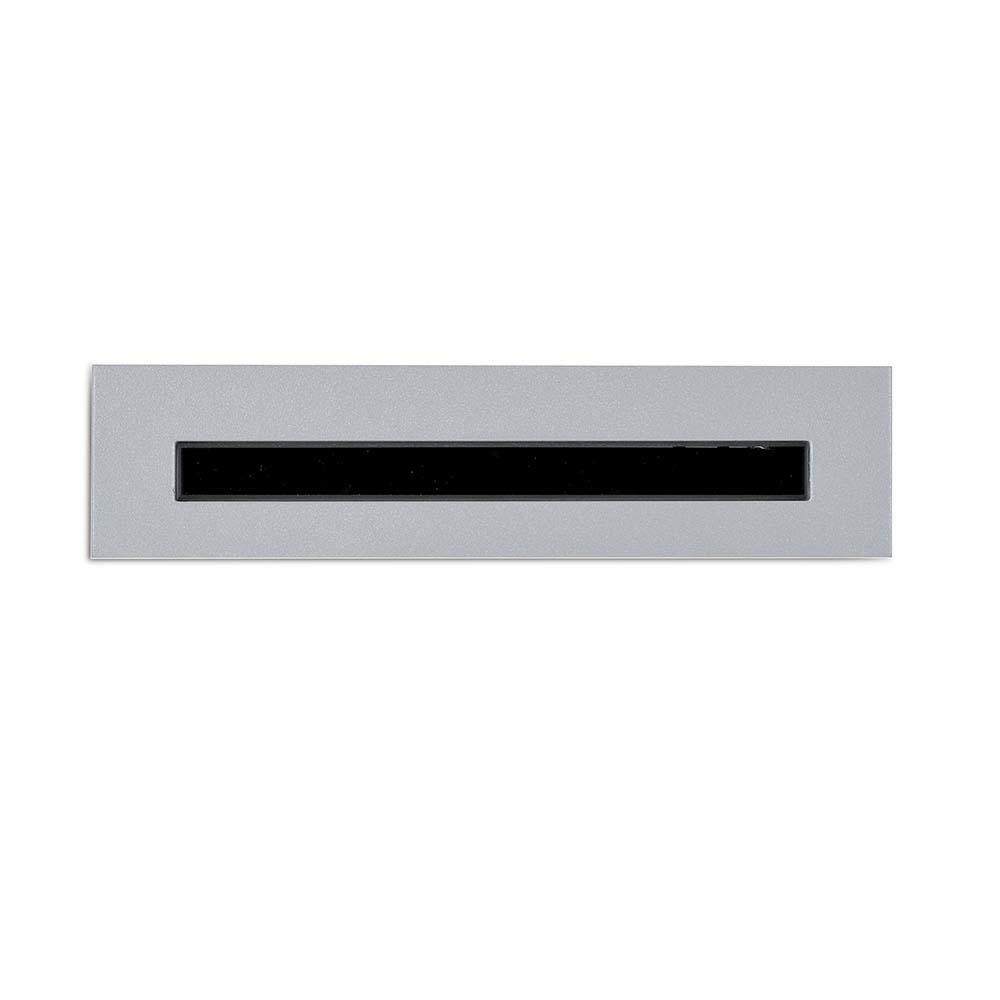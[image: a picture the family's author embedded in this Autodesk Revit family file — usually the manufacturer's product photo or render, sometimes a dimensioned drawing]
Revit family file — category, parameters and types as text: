
# Revit family: Platek_Frame
name_source: partatom
category: Apparecchi per illuminazione
revit_build: Autodesk Revit 2017 (Build: 20160225_1515(x64)
units: mm (PartAtom-declared; Revit-internal decimal feet)

## family parameters
Condiviso = No
Host = Superficie
Punto di calcolo locali = No
Quota connettore circolare = Usa diametro
Sorgente d'illuminazione = Sì
Taglio con vuoti quando caricato = Sì
Tipo di parte = Normale

## types (1)
- 3455911_4,8W_LED_3000K
    Angolo inclinazione = -90.00°
    Body = PLK_06_Grey
    CRI = >80
    Cable Lenght = Cable length 0,2 m(3x1mm2)
    Carico apparente = 0 VA
    Codice assieme = 3455911.06(Grey);3455911.01(Black);3455911.02(White);3455911.07(Corten);3455911.08(Anthracite);3455911.09(Bronze)
    Colour Temperature = 3000 K
    Commenti sul tipo = Paths, Ramps, Steps
    Descrizione = Outdoor Lighting, Wall mounted
    Diffuse Type = GLASS
    Dimmable = NO
    Emetti da larghezza rettangolo = 1 mm  [stored 0.00328084 ft]
    Emetti da lunghezza rettangolo = 163 mm  [stored 0.534777 ft]
    Energy Efficiency Rating = A/A+/A++
    File diagramma fotometrico = 3480119.IES
    Filtro dei colori = 16777215
    Frequency = 50/60Hz
    IK Rating = IK08
    IP Rating = IP65
    Immagine tipo = frame_1_ph_original.jpg
    Insulation Class = 1
    LED Protection = Surge Protection Included
    Lampada = LED
    Light Source = PLK_Light Source
    Luminaire Luminous Flux = 145 lm
    Luminaire Luminous Intensity = 120 cd
    Luminare Wattage = 5 VA
    Manufacturer Comment = 5mm flat tempered glass
    Modello = FRAME
    Mounting Type = Wall Recessed
    Nota chiave = Other LED colors available on request
    PLATEK Article Code = 3455911+9920050(Recessed Box)
    Part Body = PLK_Plastic_Black
    Power Supply Unit = Included
    Product Dimension = L205mm x W50 mm x H72mm
    Product Documentation Link = http://www.platek.eu
    Product Page URL = http://www.platek.eu
    Produttore = PLATEK SRL
    Prospetto di default = 1219 mm
    Recessed Box = PLK_Plastic_Black
    Rendi la forma visibile nel rendering = No
    Supply Voltage = 230 V
    Supply Voltage Max = 240 V
    Supply Voltage Min = 220 V
    URL = www.platek.eu
    Variazione temperatura colore lampada con luminosità attenuata = <Nessuno>

note: [stored X ft] marks values corroborated as IEEE doubles in the binary element streams (Revit-internal decimal feet)
